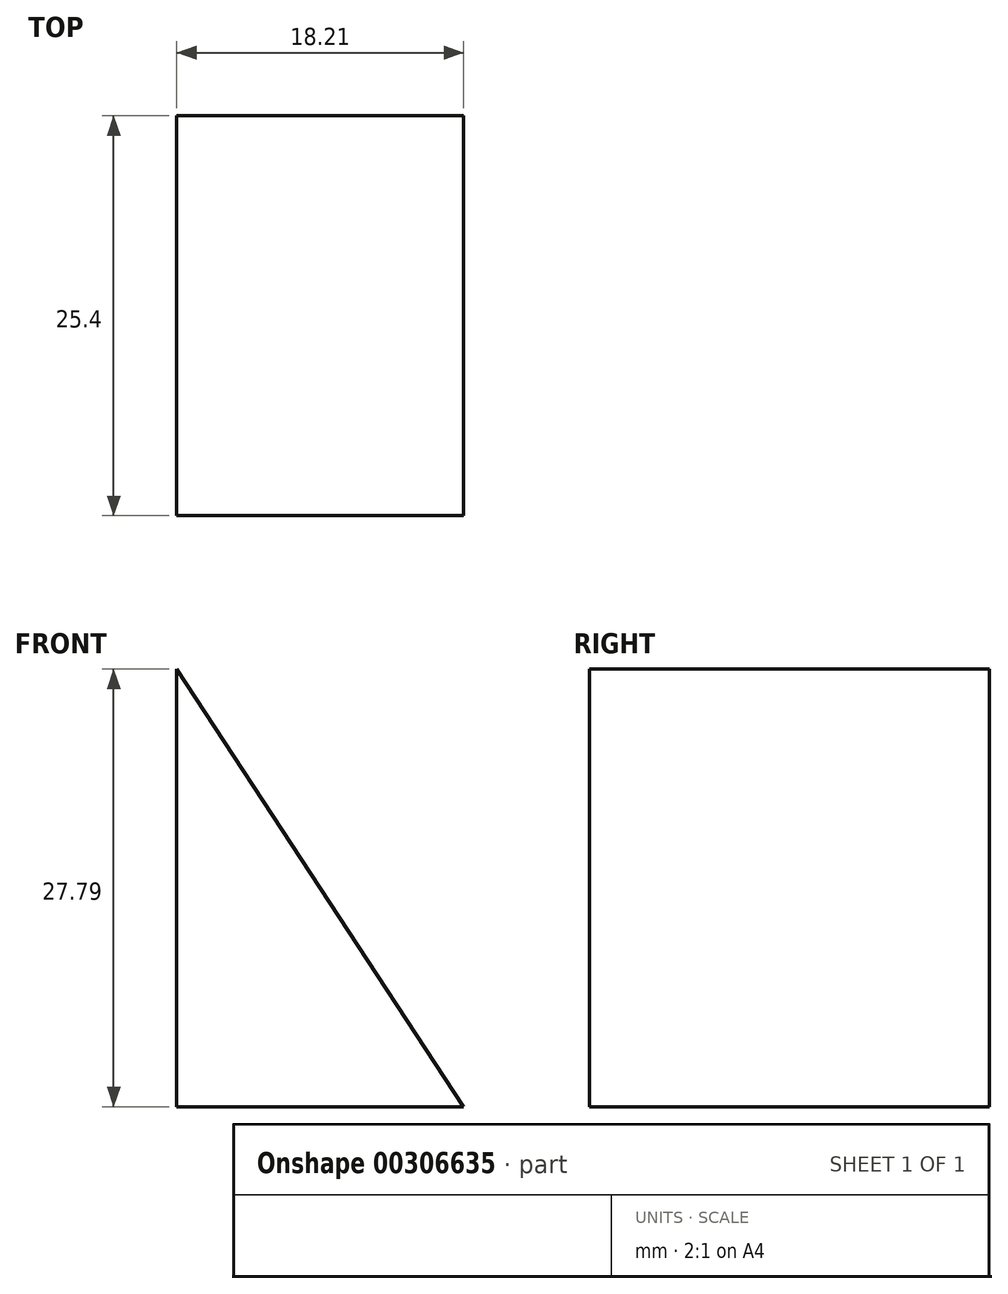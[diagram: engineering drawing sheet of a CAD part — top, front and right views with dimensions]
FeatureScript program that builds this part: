
annotation { "Feature Type Name" : "Feature", "Feature Type Description" : "" }
export const myFeature = defineFeature(function(context is Context, id is Id, definition is map)
    precondition{}
    {
        {
            var Q0;
            Q0=qCreatedBy(makeId("Front.planeOp"),FACE);
            var sketch = newSketch(context, id + "F0", { "sketchPlane" : qUnion([Q0])});
            skLineSegment(sketch, "E0", {"start": v(-53.02, 36.9) * mm, "end": v(-53.02, 9.1) * mm});
            skLineSegment(sketch, "E1", {"start": v(-53.02, 9.1) * mm, "end": v(-34.81, 9.1) * mm});
            skLineSegment(sketch, "E2", {"start": v(-53.02, 36.9) * mm, "end": v(-34.81, 9.1) * mm});
            skSolve(sketch);
        }
        {
            var Q0;
            Q0 = qSketchRegion(id + "F0", true);
            extrude(context, id + "F1", {"entities" : qUnion([Q0]), "depth" : 25.4 * mm});
        }
    });
